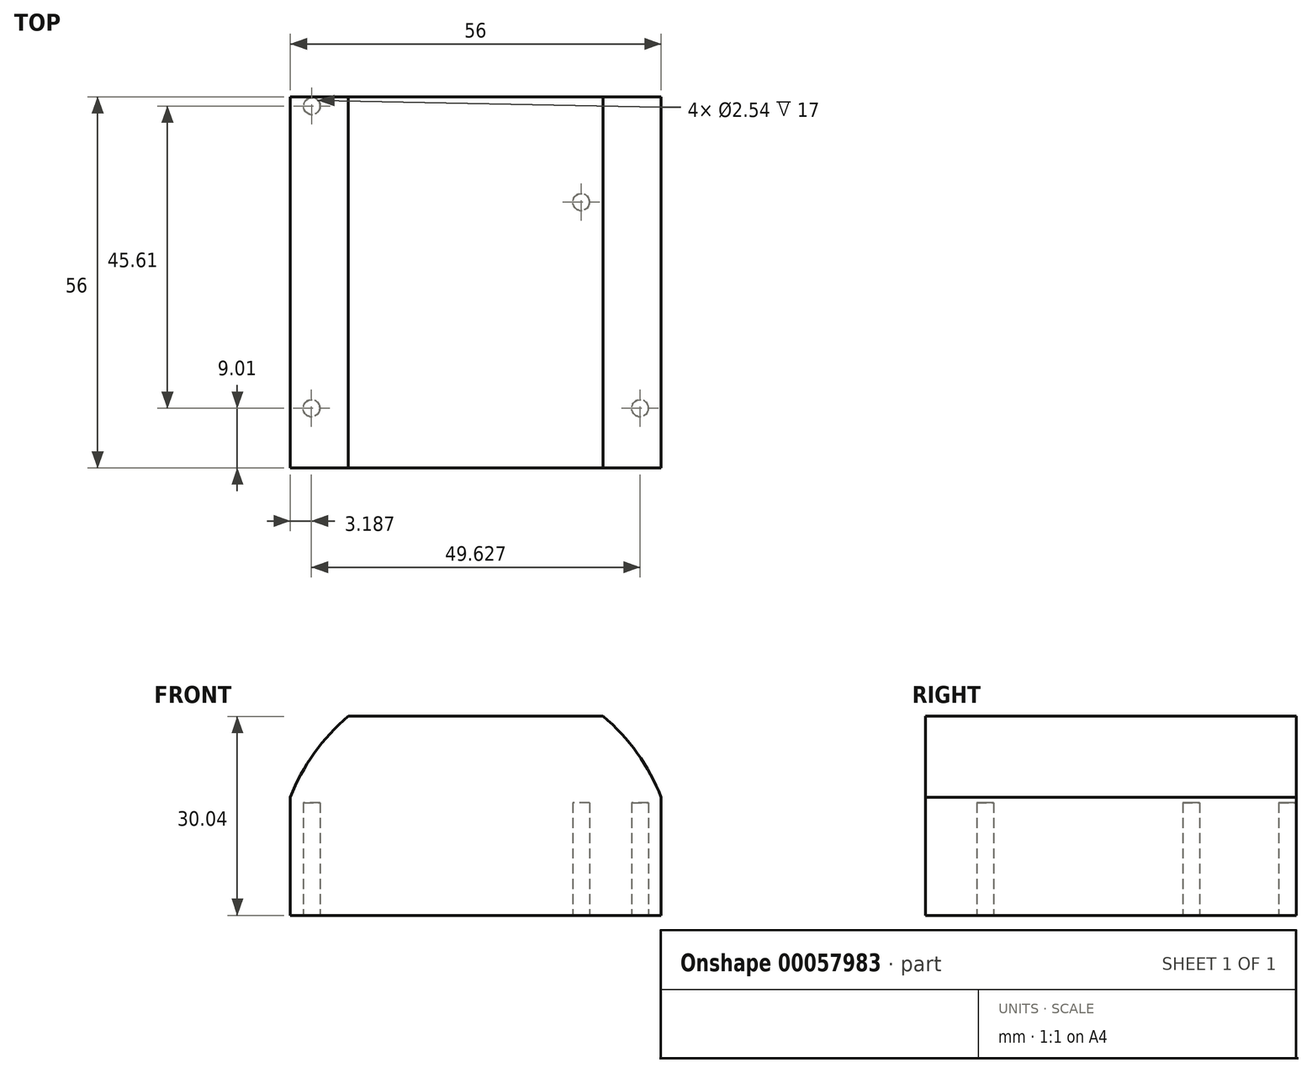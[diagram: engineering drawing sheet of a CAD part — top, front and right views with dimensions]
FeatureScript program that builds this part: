
annotation { "Feature Type Name" : "Feature", "Feature Type Description" : "" }
export const myFeature = defineFeature(function(context is Context, id is Id, definition is map)
    precondition{}
    {
        {
            var Q0;
            Q0=qCreatedBy(makeId("Top.planeOp"),FACE);
            var sketch = newSketch(context, id + "F0", { "sketchPlane" : qUnion([Q0])});
            skLineSegment(sketch, "E0.rect.bottom", {"start": v(24.84, -24.91) * mm, "end": v(-24.84, -24.91) * mm});
            skLineSegment(sketch, "E0.rect.top", {"start": v(24.84, 24.91) * mm, "end": v(-24.84, 24.91) * mm});
            skLineSegment(sketch, "E0.rect.left", {"start": v(24.84, -24.91) * mm, "end": v(24.84, 24.9) * mm});
            skPoint(sketch, "E0.rect.middle", {"position": v(0, 0) * mm});
            skCircle(sketch, "E1", {"center": v(-24.81, -18.99) * mm, "radius": 1.27 * mm});
            skCircle(sketch, "E2", {"center": v(-24.76, 26.62) * mm, "radius": 1.27 * mm});
            skCircle(sketch, "E3", {"center": v(15.91, 12.13) * mm, "radius": 1.27 * mm});
            skLineSegment(sketch, "E4", {"start": v(0, -24.91) * mm, "end": v(0, -18.21) * mm});
            skCircle(sketch, "E5.MirrorC", {"center": v(24.81, -18.99) * mm, "radius": 1.27 * mm});
            skLineSegment(sketch, "E6.rect.bottom", {"start": v(26.75, -26.75) * mm, "end": v(-26.75, -26.75) * mm});
            skLineSegment(sketch, "E6.rect.top", {"start": v(26.75, 26.75) * mm, "end": v(-26.75, 26.75) * mm});
            skLineSegment(sketch, "E6.rect.left", {"start": v(26.75, -26.75) * mm, "end": v(26.75, 26.75) * mm});
            skLineSegment(sketch, "E6.rect.right", {"start": v(-26.75, -26.75) * mm, "end": v(-26.75, 26.75) * mm});
            skLineSegment(sketch, "E7.rect.bottom", {"start": v(28, -28) * mm, "end": v(-28, -28) * mm});
            skLineSegment(sketch, "E7.rect.top", {"start": v(28, 28) * mm, "end": v(-28, 28) * mm});
            skLineSegment(sketch, "E7.rect.left", {"start": v(28, -28) * mm, "end": v(28, 28) * mm});
            skLineSegment(sketch, "E7.rect.right", {"start": v(-28, -28) * mm, "end": v(-28, 28) * mm});
            skPoint(sketch, "E8", {"position": v(8.65, 14) * mm});
            skSolve(sketch);
        }
        {
            var Q0;
            Q0=qSketchRegion(id+"F0",true);
            var Q1;
            Q1=makeQuery(id+"F0.imprint","IMPRINT",FACE,{"disambiguationData":[TD([[makeQuery(id+"F0.imprint","IMPRINT",EDGE,{"derivedFrom":sQuery(id+"F0.wireOp",EDGE,"E1")}),-1.0]])]});
            extrude(context, id + "F1", {"entities" : qUnion([Q0, Q1]), "depth" : 35 * mm});
        }
        {
            var Q0;
            Q0=makeQuery(id+"F1.opExtrude","CAP_FACE",FACE,{"disambiguationData":[OSD([sQuery(id+"F0.wireOp",EDGE,"E1"),sQuery(id+"F0.wireOp",EDGE,"E2"),sQuery(id+"F0.wireOp",EDGE,"E3"),sQuery(id+"F0.wireOp",EDGE,"E5.MirrorC"),sQuery(id+"F0.wireOp",EDGE,"E7.rect.bottom"),sQuery(id+"F0.wireOp",EDGE,"E7.rect.top"),sQuery(id+"F0.wireOp",EDGE,"E7.rect.left"),sQuery(id+"F0.wireOp",EDGE,"E7.rect.right")])],"isStart":false});
            cPlane(context, id + "F2", {"entities" : qUnion([Q0]), "cplaneType" : CPlaneType.OFFSET, "offset" : 0 * mm, "width" : 150 * mm, "height" : 150 * mm});
        }
        {
            var Q0;
            Q0=qCreatedBy(id+"F2.planeOp",FACE);
            var sketch = newSketch(context, id + "F3", { "sketchPlane" : qUnion([Q0])});
            skPoint(sketch, "E9.rect.middle", {"position": v(0, 0) * mm});
            skCircle(sketch, "E10", {"center": v(-24.81, -18.99) * mm, "radius": 1.27 * mm});
            skCircle(sketch, "E11", {"center": v(-24.76, 26.62) * mm, "radius": 1.27 * mm});
            skCircle(sketch, "E12", {"center": v(15.91, 12.13) * mm, "radius": 1.27 * mm});
            skCircle(sketch, "E13.MirrorC", {"center": v(24.81, -18.99) * mm, "radius": 1.27 * mm});
            skPoint(sketch, "E14", {"position": v(8.65, 14) * mm});
            skSolve(sketch);
        }
        {
            var Q0;
            Q0 = qSketchRegion(id + "F3", true);
            extrude(context, id + "F4", {"entities" : qUnion([Q0]), "operationType" : NewBodyOperationType.ADD, "oppositeDirection" : true, "depth" : 18 * mm});
        }
        {
            var Q0;
            Q0=qCreatedBy(makeId("Front.planeOp"),FACE);
            var sketch = newSketch(context, id + "F5", { "sketchPlane" : qUnion([Q0])});
            skLineSegment(sketch, "E15", {"start": v(0, 0) * mm, "end": v(0, 7) * mm});
            skLineSegment(sketch, "E16", {"start": v(0, 7) * mm, "end": v(30.01, 7) * mm});
            skLineSegment(sketch, "E17", {"start": v(30.01, 7) * mm, "end": v(30.01, 25.5) * mm});
            skLineSegment(sketch, "E18", {"start": v(15.3, 7) * mm, "end": v(30.01, 7) * mm});
            skLineSegment(sketch, "E19", {"start": v(0, 7) * mm, "end": v(-30.01, 7) * mm});
            skLineSegment(sketch, "E20", {"start": v(-30.01, 7) * mm, "end": v(-23.63, 25.5) * mm});
            skLineSegment(sketch, "E21", {"start": v(-23.63, 25.5) * mm, "end": v(-2.39, 25.5) * mm});
            skFitSpline(sketch, "E22", {"points": [v(-2.39, 25.5) * mm, v(9.33, 17.59) * mm, v(22.47, 7) * mm], "startDerivative": vector(24.35, -15.7) * mm, "endDerivative": vector(25.35, -21.24) * mm});
            skLineSegment(sketch, "E23", {"start": v(30.01, 25.5) * mm, "end": v(-2.39, 25.5) * mm});
            skLineSegment(sketch, "E24", {"start": v(-23.63, 25.5) * mm, "end": v(-30.01, 25.5) * mm});
            skLineSegment(sketch, "E25", {"start": v(-30.01, 25.5) * mm, "end": v(-30.01, 7) * mm});
            skCircle(sketch, "E26", {"center": v(0, 7) * mm, "radius": 30.01 * mm});
            skLineSegment(sketch, "E27", {"start": v(-19.23, 30.04) * mm, "end": v(19.23, 30.04) * mm});
            skLineSegment(sketch, "E28", {"start": v(-30.01, 25.5) * mm, "end": v(-30.01, 35.8) * mm});
            skLineSegment(sketch, "E29", {"start": v(-30.01, 35.8) * mm, "end": v(30.01, 35.8) * mm});
            skLineSegment(sketch, "E30", {"start": v(30.01, 35.8) * mm, "end": v(30.01, 25.5) * mm});
            skSolve(sketch);
        }
        {
            var Q0;
            {var subQ0=sQuery(id+"F5.wireOp",EDGE,"E27");Q0=makeQuery(id+"F5.imprint","IMPRINT",FACE,{"disambiguationData":[TD([[makeQuery(id+"F5.imprint","IMPRINT",EDGE,{"derivedFrom":subQ0}),1.0]])]});}
            var Q1;
            {var subQ5=sQuery(id+"F5.wireOp",EDGE,"E24");Q1=makeQuery(id+"F5.imprint","IMPRINT",FACE,{"disambiguationData":[TD([[makeQuery(id+"F5.imprint","IMPRINT",EDGE,{"derivedFrom":subQ5}),-1.0]])]});}
            var Q2;
            {var subQ0=sQuery(id+"F5.wireOp",EDGE,"E24");Q2=makeQuery(id+"F5.imprint","IMPRINT",FACE,{"disambiguationData":[TD([[makeQuery(id+"F5.imprint","IMPRINT",EDGE,{"derivedFrom":subQ0}),1.0]])]});}
            var Q3;
            {var subQ6=sQuery(id+"F5.wireOp",EDGE,"E30");Q3=makeQuery(id+"F5.imprint","IMPRINT",FACE,{"disambiguationData":[TD([[makeQuery(id+"F5.imprint","IMPRINT",EDGE,{"derivedFrom":subQ6}),-1.0]])]});}
            var Q4;
            {var subQ0=sQuery(id+"F5.wireOp",EDGE,"E17");Q4=makeQuery(id+"F5.imprint","IMPRINT",FACE,{"disambiguationData":[TD([[makeQuery(id+"F5.imprint","IMPRINT",EDGE,{"derivedFrom":subQ0}),1.0]])]});}
            extrude(context, id + "F6", {"entities" : qUnion([Q0, Q1, Q2, Q3, Q4]), "operationType" : NewBodyOperationType.REMOVE, "endBound" : BoundingType.THROUGH_ALL, "oppositeDirection" : true, "depth" : 25 * mm, "hasSecondDirection" : true, "secondDirectionBound" : SecondDirectionBoundingType.THROUGH_ALL, "secondDirectionOppositeDirection" : false, "secondDirectionDepth" : 25 * mm});
        }
    });
